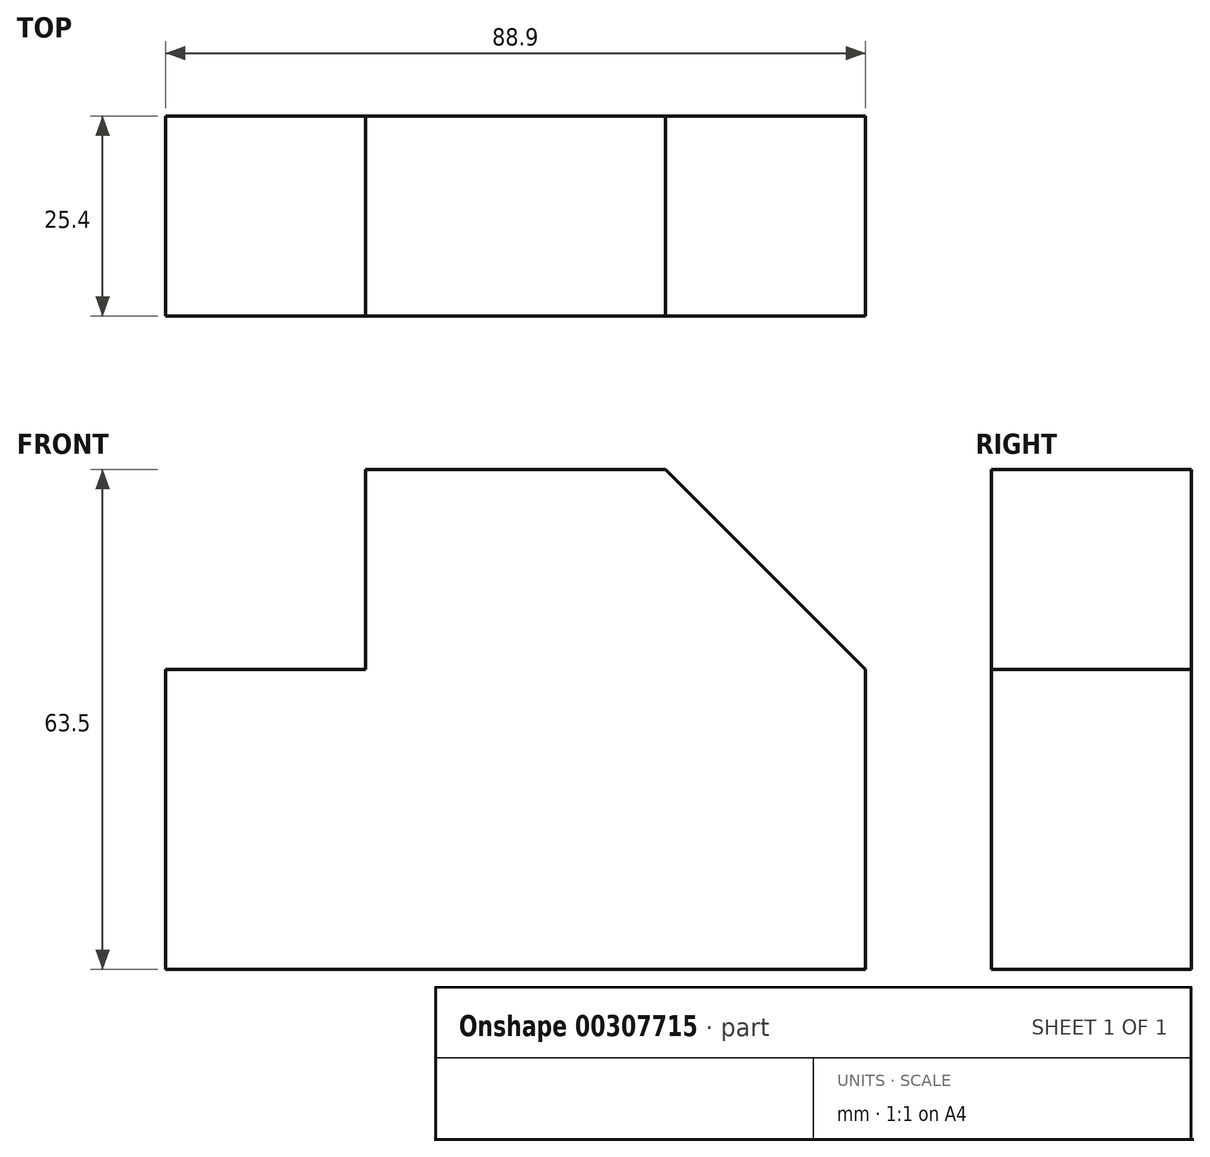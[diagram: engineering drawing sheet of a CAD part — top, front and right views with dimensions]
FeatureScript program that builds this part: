
annotation { "Feature Type Name" : "Feature", "Feature Type Description" : "" }
export const myFeature = defineFeature(function(context is Context, id is Id, definition is map)
    precondition{}
    {
        {
            var Q0;
            Q0=qCreatedBy(makeId("Front.planeOp"),FACE);
            var sketch = newSketch(context, id + "F0", { "sketchPlane" : qUnion([Q0])});
            skLineSegment(sketch, "E0", {"start": v(-41.75, -58.5) * mm, "end": v(47.15, -58.5) * mm});
            skLineSegment(sketch, "E1", {"start": v(47.15, -58.5) * mm, "end": v(47.15, -20.4) * mm});
            skLineSegment(sketch, "E2", {"start": v(-41.75, -58.5) * mm, "end": v(-41.75, -20.4) * mm});
            skLineSegment(sketch, "E3", {"start": v(-41.75, -20.4) * mm, "end": v(-16.35, -20.4) * mm});
            skLineSegment(sketch, "E4", {"start": v(-16.35, -20.4) * mm, "end": v(-16.35, 5) * mm});
            skLineSegment(sketch, "E5", {"start": v(-16.35, 5) * mm, "end": v(21.75, 5) * mm});
            skLineSegment(sketch, "E6", {"start": v(21.75, 5) * mm, "end": v(47.15, -20.4) * mm});
            skSolve(sketch);
        }
        {
            var Q0;
            Q0=makeQuery(id+"F0.imprint","IMPRINT",FACE,{"disambiguationData":[TD([[makeQuery(id+"F0.imprint","IMPRINT",EDGE,{"derivedFrom":sQuery(id+"F0.wireOp",EDGE,"E0")}),1.0]])]});
            extrude(context, id + "F1", {"entities" : qUnion([Q0]), "depth" : 25.4 * mm});
        }
    });
